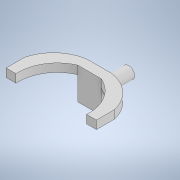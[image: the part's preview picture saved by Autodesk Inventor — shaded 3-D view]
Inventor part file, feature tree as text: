
AUTODESK INVENTOR PART (.ipt)
format: ipt  version: 2022 (Build 260153000, 153)  size: 142,336 bytes
history: native  units: in
note: dims shown in document units (in); Inventor stores cm internally (conversion verified against a paired STEP export)
features: extrude x3, sketch x3
ambient origin geometry x8: Origin, YZ Plane, XZ Plane, XY Plane, X Axis, Y Axis, Z Axis, Center Point
bodies: Solid1 (feature_tree)
feature tree (6):
  extrude  "Extrusion1"  Depth=1.1811in TaperAngle=0.0deg
  extrude  "Extrusion2"  Depth=0.4724in
  extrude  "Extrusion3"  Depth=0.3312in
  sketch  "Sketch1"  dims[d0=0.4724in d1=1.1811in d2=0.0in]
  sketch  "Sketch2"  dims[d3=0.4724in d4=0.4724in]
  sketch  "Sketch3"  dims[d5=0.4724in d6=0.4724in d7=0.3937in d8=0.0in d9=0.9449in d10=0.9449in d11=1.5748in d12=0.9449in d13=1.5748in d14=0.3937in d15=0.3937in d16=1.5748in d17=1.5748in d18=0.3312in d19=0.0in]
